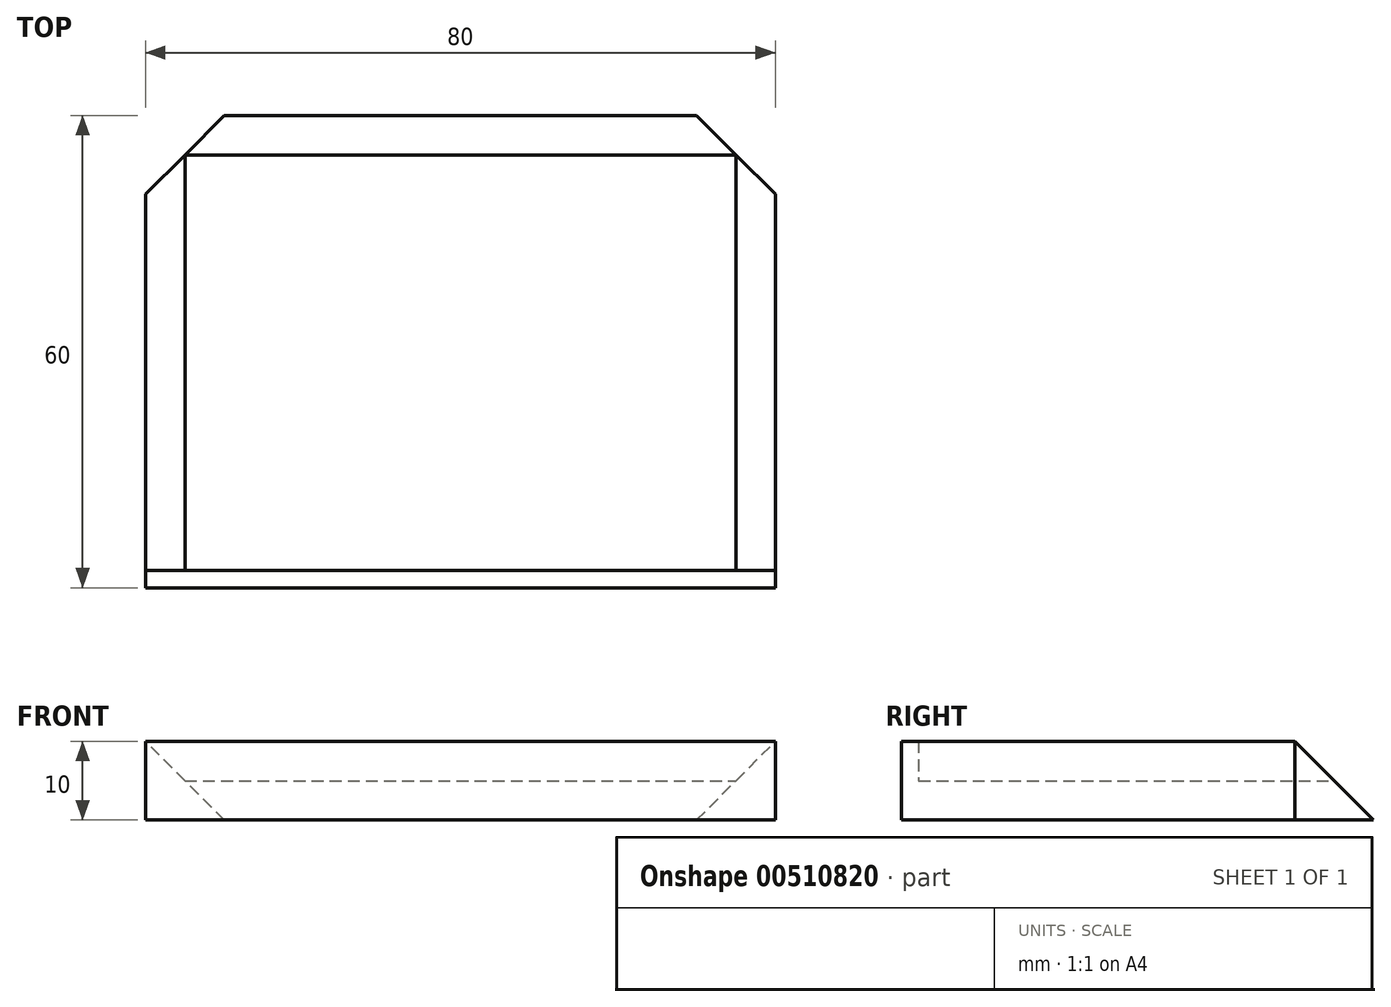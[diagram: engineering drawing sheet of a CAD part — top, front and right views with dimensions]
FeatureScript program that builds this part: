
annotation { "Feature Type Name" : "Feature", "Feature Type Description" : "" }
export const myFeature = defineFeature(function(context is Context, id is Id, definition is map)
    precondition{}
    {
        {
            var Q0;
            Q0=qCreatedBy(makeId("Top.planeOp"),FACE);
            var sketch = newSketch(context, id + "F0", { "sketchPlane" : qUnion([Q0])});
            skLineSegment(sketch, "E0", {"start": v(-27.76, 22.82) * mm, "end": v(32.24, 22.82) * mm});
            skLineSegment(sketch, "E1", {"start": v(32.24, 22.82) * mm, "end": v(42.24, 12.82) * mm});
            skLineSegment(sketch, "E2", {"start": v(42.24, 12.82) * mm, "end": v(42.24, -37.18) * mm});
            skLineSegment(sketch, "E3", {"start": v(42.24, -37.18) * mm, "end": v(-37.76, -37.18) * mm});
            skLineSegment(sketch, "E4", {"start": v(-37.76, -37.18) * mm, "end": v(-37.76, 12.82) * mm});
            skLineSegment(sketch, "E5", {"start": v(-37.76, 12.82) * mm, "end": v(-27.76, 22.82) * mm});
            skSolve(sketch);
        }
        {
            var Q0;
            Q0=makeQuery(id+"F0.imprint","IMPRINT",FACE,{"disambiguationData":[TD([[makeQuery(id+"F0.imprint","IMPRINT",EDGE,{"derivedFrom":sQuery(id+"F0.wireOp",EDGE,"E0")}),-1.0]])]});
            extrude(context, id + "F1", {"entities" : qUnion([Q0]), "depth" : 10 * mm, "offsetDistance" : 25 * mm});
        }
        {
            var Q0;
            Q0=qCreatedBy(makeId("Right.planeOp"),FACE);
            var sketch = newSketch(context, id + "F2", { "sketchPlane" : qUnion([Q0])});
            skPoint(sketch, "E6.0", {"position": v(22.82, 10) * mm});
            skPoint(sketch, "E7.0", {"position": v(22.82, 0) * mm});
            skLineSegment(sketch, "E8", {"start": v(22.82, 10) * mm, "end": v(12.82, 10) * mm});
            skLineSegment(sketch, "E9", {"start": v(12.82, 10) * mm, "end": v(22.82, 0) * mm});
            skLineSegment(sketch, "E10", {"start": v(22.82, 10) * mm, "end": v(22.82, 0) * mm});
            skSolve(sketch);
        }
        {
            var Q0;
            Q0 = qSketchRegion(id + "F2", true);
            extrude(context, id + "F3", {"entities" : qUnion([Q0]), "operationType" : NewBodyOperationType.REMOVE, "endBound" : BoundingType.THROUGH_ALL, "depth" : 25 * mm, "offsetDistance" : 25 * mm});
        }
        {
            var Q0;
            Q0 = qSketchRegion(id + "F2", true);
            extrude(context, id + "F4", {"entities" : qUnion([Q0]), "operationType" : NewBodyOperationType.REMOVE, "endBound" : BoundingType.THROUGH_ALL, "oppositeDirection" : true, "depth" : 25 * mm});
        }
        {
            var Q0;
            Q0=qCreatedBy(makeId("Front.planeOp"),FACE);
            var sketch = newSketch(context, id + "F5", { "sketchPlane" : qUnion([Q0])});
            skPoint(sketch, "E11.0", {"position": v(42.24, 10) * mm});
            skPoint(sketch, "E12.0", {"position": v(-37.76, 10) * mm});
            skPoint(sketch, "E13.0", {"position": v(37.24, 5) * mm});
            skPoint(sketch, "E14.0", {"position": v(-32.76, 5) * mm});
            skLineSegment(sketch, "E15", {"start": v(42.24, 10) * mm, "end": v(-37.76, 10) * mm});
            skLineSegment(sketch, "E16", {"start": v(-32.76, 5) * mm, "end": v(-37.76, 10) * mm});
            skLineSegment(sketch, "E17", {"start": v(42.24, 10) * mm, "end": v(37.24, 5) * mm});
            skLineSegment(sketch, "E18", {"start": v(37.24, 5) * mm, "end": v(-32.76, 5) * mm});
            skSolve(sketch);
        }
        {
            var Q0;
            Q0 = qSketchRegion(id + "F5", true);
            var Q1;
            Q1 = qConstructionFilter(qBodyType(qCreatedBy(id + "F5" ,EDGE), BodyType.WIRE), ConstructionObject.NO);
            extrude(context, id + "F6", {"entities" : qUnion([Q0]), "operationType" : NewBodyOperationType.REMOVE, "surfaceEntities" : qUnion([Q1]), "depth" : 35 * mm, "offsetDistance" : 25 * mm});
        }
        {
            var Q0;
            Q0 = qSketchRegion(id + "F5", true);
            extrude(context, id + "F7", {"entities" : qUnion([Q0]), "operationType" : NewBodyOperationType.REMOVE, "oppositeDirection" : true, "depth" : 25 * mm, "offsetDistance" : 25 * mm});
        }
    });
